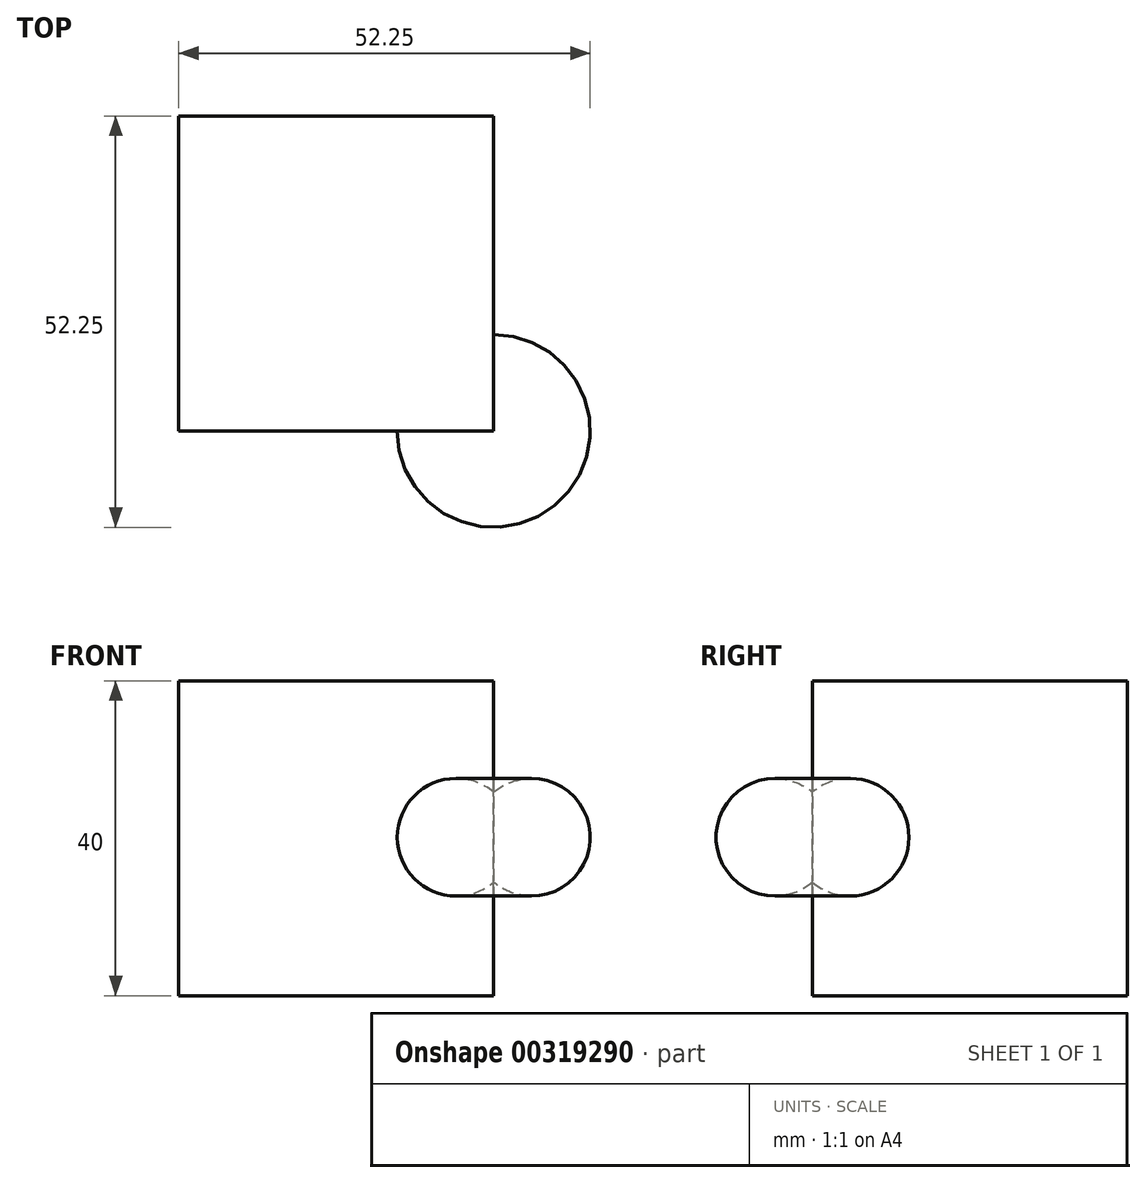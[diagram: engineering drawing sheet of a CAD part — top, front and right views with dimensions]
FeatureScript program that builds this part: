
annotation { "Feature Type Name" : "Feature", "Feature Type Description" : "" }
export const myFeature = defineFeature(function(context is Context, id is Id, definition is map)
    precondition{}
    {
        {
            var Q0;
            Q0=qCreatedBy(makeId("Front.planeOp"),FACE);
            var sketch = newSketch(context, id + "F0", { "sketchPlane" : qUnion([Q0])});
            skLineSegment(sketch, "E0.bottom", {"start": v(0, 0) * mm, "end": v(40, 0) * mm});
            skLineSegment(sketch, "E0.top", {"start": v(0, 40) * mm, "end": v(40, 40) * mm});
            skLineSegment(sketch, "E0.left", {"start": v(0, 0) * mm, "end": v(0, 40) * mm});
            skLineSegment(sketch, "E0.right", {"start": v(40, 0) * mm, "end": v(40, 40) * mm});
            skSolve(sketch);
        }
        {
            var Q0;
            Q0 = qSketchRegion(id + "F0", true);
            extrude(context, id + "F1", {"entities" : qUnion([Q0]), "depth" : 40 * mm});
        }
        {
            var Q0;
            Q0=makeQuery(id+"F1.opExtrude","CAP_FACE",FACE,{"disambiguationData":[OSD([sQuery(id+"F0.wireOp",EDGE,"E0.bottom"),sQuery(id+"F0.wireOp",EDGE,"E0.top"),sQuery(id+"F0.wireOp",EDGE,"E0.left"),sQuery(id+"F0.wireOp",EDGE,"E0.right")])],"isStart":false});
            var sketch = newSketch(context, id + "F2", { "sketchPlane" : qUnion([Q0])});
            skPoint(sketch, "E1", {"position": v(40, 25.86) * mm});
            skPoint(sketch, "E2", {"position": v(40, 14.4) * mm});
            skLineSegment(sketch, "E3", {"start": v(40, 25.86) * mm, "end": v(40, 14.4) * mm});
            skArc(sketch, "E4", {"start": v(40, 14.4) * mm, "mid": v(52.25, 20.12) * mm, "end": v(40, 25.86) * mm});
            skSolve(sketch);
        }
        {
            var Q0;
            Q0=makeQuery(id+"F2.imprint","IMPRINT",FACE,{"disambiguationData":[TD([[makeQuery(id+"F2.imprint","IMPRINT",EDGE,{"derivedFrom":sQuery(id+"F2.wireOp",EDGE,"E3")}),-1.0]])]});
            var Q1;
            Q1=makeQuery(id+"F1.opExtrude","CAP_EDGE",EDGE,{"disambiguationData":[OSD([sQuery(id+"F0.wireOp",EDGE,"E0.right")])],"isStart":false});
            revolve(context, id + "F3", {"operationType" : NewBodyOperationType.ADD, "entities" : qUnion([Q0]), "axis" : qUnion([Q1]), "revolveType" : RevolveType.FULL});
        }
    });
